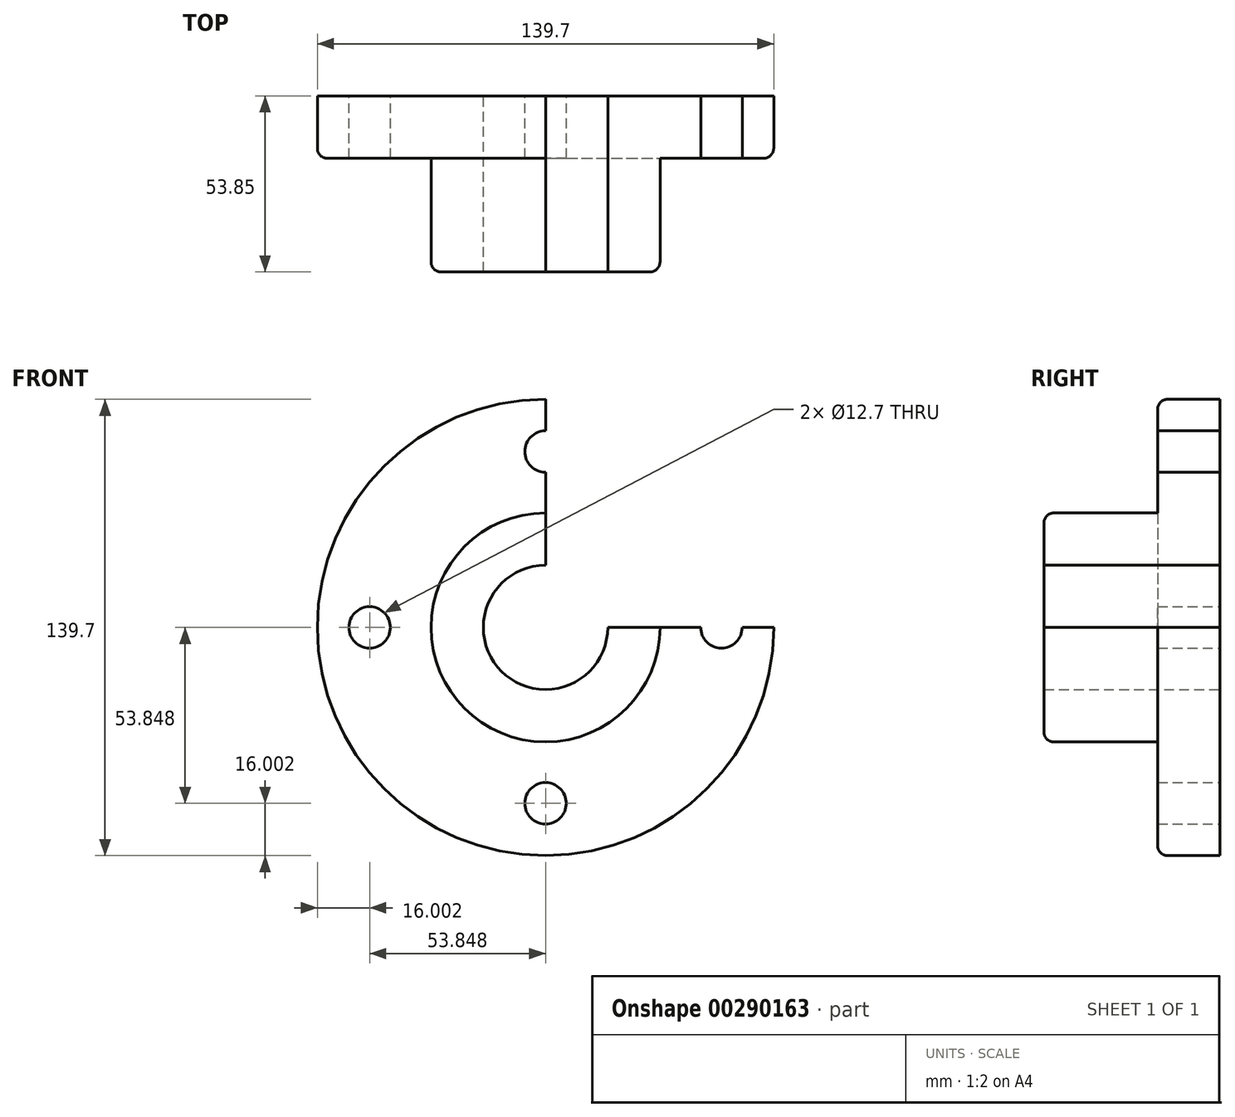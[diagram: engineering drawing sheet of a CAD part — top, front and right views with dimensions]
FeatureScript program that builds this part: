
annotation { "Feature Type Name" : "Feature", "Feature Type Description" : "" }
export const myFeature = defineFeature(function(context is Context, id is Id, definition is map)
    precondition{}
    {
        {
            var Q0;
            Q0=qCreatedBy(makeId("Front.planeOp"),FACE);
            var sketch = newSketch(context, id + "F0", { "sketchPlane" : qUnion([Q0])});
            skCircle(sketch, "E0", {"center": v(0, 0) * mm, "radius": 35.05 * mm});
            skCircle(sketch, "E1", {"center": v(0, 0) * mm, "radius": 53.85 * mm});
            skCircle(sketch, "E2", {"center": v(0, 0) * mm, "radius": 69.85 * mm});
            skCircle(sketch, "E3", {"center": v(0, 0) * mm, "radius": 19.05 * mm});
            skCircle(sketch, "E4", {"center": v(0, 53.85) * mm, "radius": 6.35 * mm});
            skCircle(sketch, "E5", {"center": v(53.85, 0) * mm, "radius": 6.35 * mm});
            skCircle(sketch, "E6", {"center": v(0, -53.85) * mm, "radius": 6.35 * mm});
            skCircle(sketch, "E7", {"center": v(-53.85, 0) * mm, "radius": 6.35 * mm});
            skSolve(sketch);
        }
        {
            var Q0;
            Q0=makeQuery(id+"F0.imprint","IMPRINT",FACE,{"disambiguationData":[TD([[makeQuery(id+"F0.imprint","IMPRINT",EDGE,{"derivedFrom":sQuery(id+"F0.wireOp",EDGE,"E0")}),1.0]])]});
            extrude(context, id + "F1", {"entities" : qUnion([Q0]), "depth" : 53.85 * mm});
        }
        {
            var Q0;
            Q0=makeQuery(id+"F0.imprint","IMPRINT",FACE,{"disambiguationData":[TD([[makeQuery(id+"F0.imprint","IMPRINT",EDGE,{"derivedFrom":sQuery(id+"F0.wireOp",EDGE,"E2")}),1.0]])]});
            var Q1;
            Q1=makeQuery(id+"F0.imprint","IMPRINT",FACE,{"disambiguationData":[TD([[makeQuery(id+"F0.imprint","IMPRINT",EDGE,{"derivedFrom":sQuery(id+"F0.wireOp",EDGE,"E0")}),-1.0]])]});
            extrude(context, id + "F2", {"entities" : qUnion([Q0, Q1]), "operationType" : NewBodyOperationType.ADD, "depth" : 19.05 * mm});
        }
        {
            var Q0;
            Q0=qCreatedBy(makeId("Front.planeOp"),FACE);
            var sketch = newSketch(context, id + "F3", { "sketchPlane" : qUnion([Q0])});
            skLineSegment(sketch, "E8.bottom", {"start": v(0, 0) * mm, "end": v(73.3, 0) * mm});
            skLineSegment(sketch, "E8.top", {"start": v(0, 72.72) * mm, "end": v(73.3, 72.72) * mm});
            skLineSegment(sketch, "E8.left", {"start": v(0, 0) * mm, "end": v(0, 72.72) * mm});
            skLineSegment(sketch, "E8.right", {"start": v(73.3, 0) * mm, "end": v(73.3, 72.72) * mm});
            skSolve(sketch);
        }
        {
            var Q0;
            Q0 = qSketchRegion(id + "F3", true);
            extrude(context, id + "F4", {"entities" : qUnion([Q0]), "operationType" : NewBodyOperationType.REMOVE, "endBound" : BoundingType.THROUGH_ALL, "oppositeDirection" : true, "depth" : 25.4 * mm});
        }
        {
            var Q0;
            Q0=qCreatedBy(makeId("Front.planeOp"),FACE);
            var sketch = newSketch(context, id + "F5", { "sketchPlane" : qUnion([Q0])});
            skLineSegment(sketch, "E9.bottom", {"start": v(0, 0) * mm, "end": v(74.89, 0) * mm});
            skLineSegment(sketch, "E9.top", {"start": v(0, 75.48) * mm, "end": v(74.89, 75.48) * mm});
            skLineSegment(sketch, "E9.left", {"start": v(0, 0) * mm, "end": v(0, 75.48) * mm});
            skLineSegment(sketch, "E9.right", {"start": v(74.89, 0) * mm, "end": v(74.89, 75.48) * mm});
            skSolve(sketch);
        }
        {
            var Q0;
            Q0 = qSketchRegion(id + "F5", true);
            extrude(context, id + "F6", {"entities" : qUnion([Q0]), "operationType" : NewBodyOperationType.REMOVE, "endBound" : BoundingType.THROUGH_ALL, "depth" : 25.4 * mm});
        }
        {
            var Q0;
            Q0=makeQuery(id+"F1.opExtrude","CAP_EDGE",EDGE,{"disambiguationData":[OSD([sQuery(id+"F0.wireOp",EDGE,"E0")])],"isStart":false});
            var Q1;
            Q1=makeQuery(id+"F2.opExtrude","CAP_EDGE",EDGE,{"disambiguationData":[OSD([sQuery(id+"F0.wireOp",EDGE,"E0")])],"isStart":false});
            var Q2;
            Q2=makeQuery(id+"F2.opExtrude","CAP_EDGE",EDGE,{"disambiguationData":[OSD([sQuery(id+"F0.wireOp",EDGE,"E2")])],"isStart":false});
            fillet(context, id + "F7", {"entities" : qUnion([Q0, Q1, Q2]), "radius" : 3.05 * mm, "tangentPropagation" : true, "allowEdgeOverflow" : false});
        }
    });
